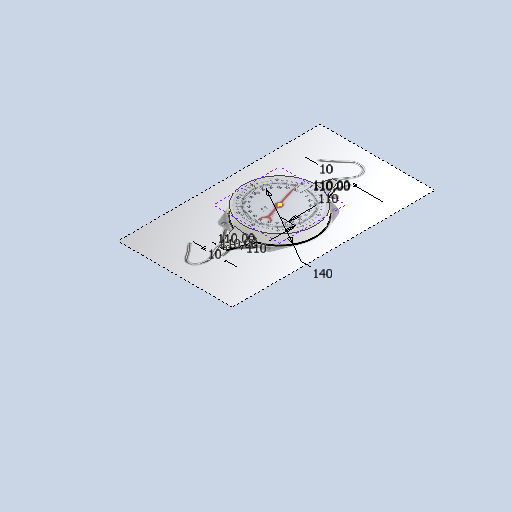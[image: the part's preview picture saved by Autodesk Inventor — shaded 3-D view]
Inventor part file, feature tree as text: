
AUTODESK INVENTOR PART (.ipt)
format: ipt  version: 2025 (Build 290162010, 162A)  size: 413,696 bytes
history: native  units: mm
features: sketch x2, extrude x2, other x2
ambient origin geometry x8: Origin, YZ Plane, XZ Plane, XY Plane, X Axis, Y Axis, Z Axis, Center Point
bodies: Volumenkörper1 (feature_tree)
feature tree (6):
  sketch  "Skizze2"  dims[d3=19.198622mm d4=19.198622mm]
  extrude  "Extrusion1"  Depth=19.198622mm
  extrude  "Extrusion2"  Depth=7.0mm
  sketch  "Skizze3"  dims[d5=110.0mm d8=140.0mm d9=110.0mm d10=19.198622mm d11=19.198622mm d12=10.0mm d13=10.0mm d22=20.0mm d23=0.0mm d24=7.0mm d25=0.0mm]
  other  "Bild1"
  other  "Bild2"
